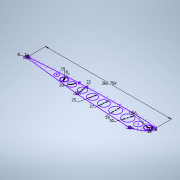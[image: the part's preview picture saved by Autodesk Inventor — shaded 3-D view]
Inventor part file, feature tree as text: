
AUTODESK INVENTOR PART (.ipt)
format: ipt  version: 2022 (Build 260153000, 153)  size: 206,336 bytes
history: native  units: mm
features: sketch x1
ambient origin geometry x8: Origin, YZ Plane, XZ Plane, XY Plane, X Axis, Y Axis, Z Axis, Center Point
feature tree (1):
  sketch  "Sketch1"  dims[d31=34.456mm d50=368.759386mm d57=16.0mm d69=8.0mm d70=20.0mm d80=19.0mm d81=16.0mm d82=1.0mm d83=1.0mm d84=1.0mm d85=1.0mm d86=1.0mm d87=0.8mm d88=1.0mm d90=19.0mm d94=5.0mm d95=5.0mm d101=5.0mm d102=5.0mm d105=5.0mm d106=5.0mm d108=2.0mm d109=22.0mm d110=30.0mm d111=29.0mm d112=27.0mm d113=25.0mm]
